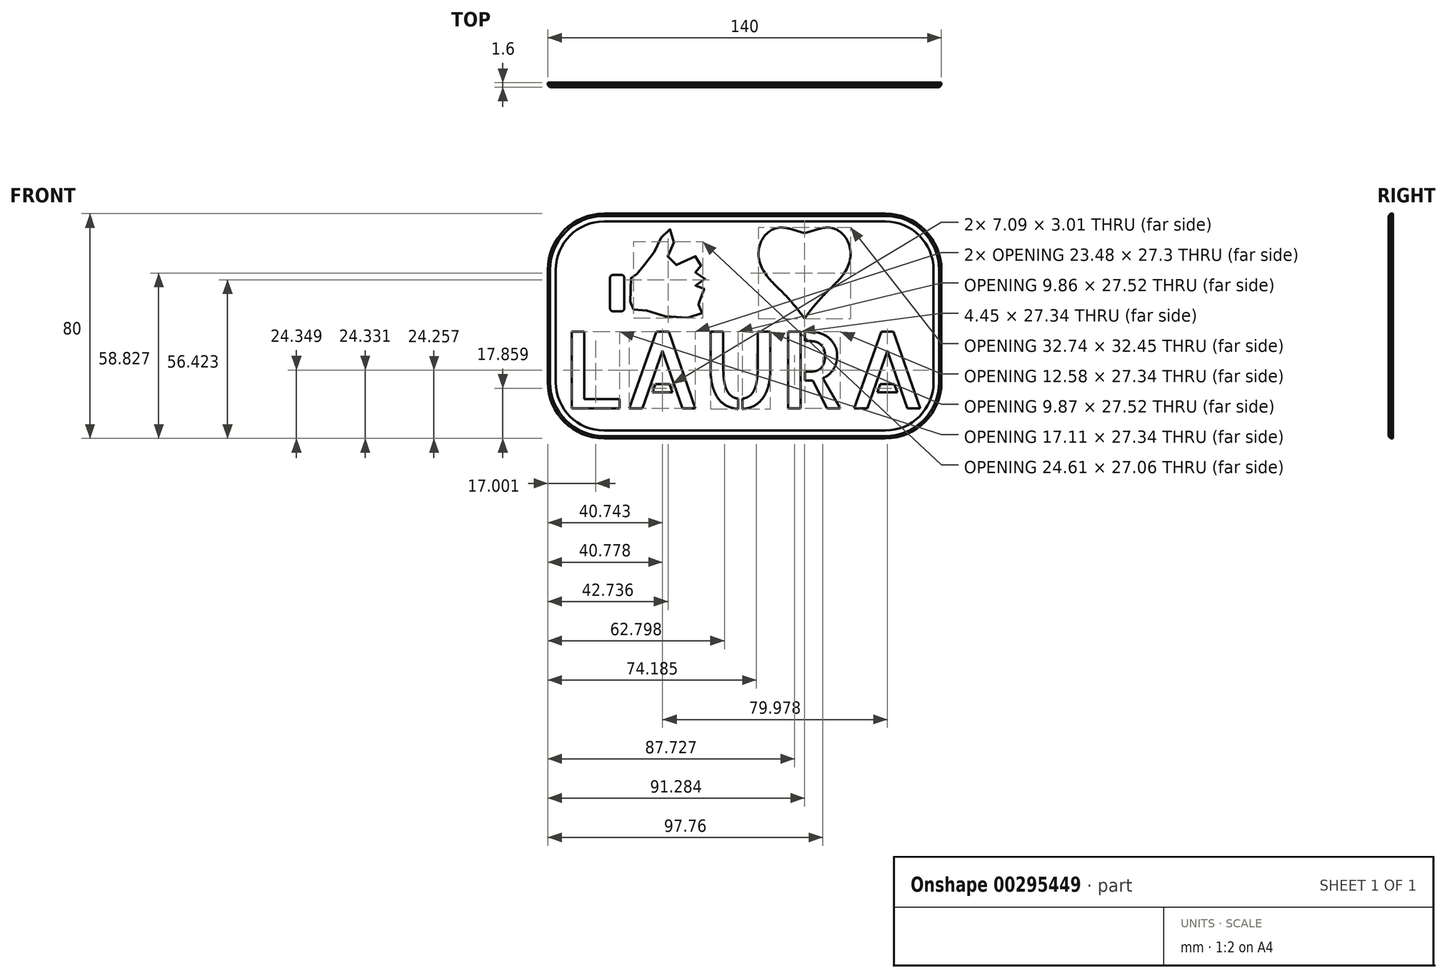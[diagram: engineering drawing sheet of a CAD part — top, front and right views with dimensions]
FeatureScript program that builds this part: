
annotation { "Feature Type Name" : "Feature", "Feature Type Description" : "" }
export const myFeature = defineFeature(function(context is Context, id is Id, definition is map)
    precondition{}
    {
        {
            var Q0;
            Q0=qCreatedBy(makeId("Front.planeOp"),FACE);
            var sketch = newSketch(context, id + "F0", { "sketchPlane" : qUnion([Q0])});
            skLineSegment(sketch, "E0.bottom", {"start": v(-70, 60) * mm, "end": v(70, 60) * mm});
            skLineSegment(sketch, "E0.top", {"start": v(-70, -20) * mm, "end": v(70, -20) * mm});
            skLineSegment(sketch, "E0.left", {"start": v(-70, 60) * mm, "end": v(-70, -20) * mm});
            skLineSegment(sketch, "E0.right", {"start": v(70, 60) * mm, "end": v(70, -20) * mm});
            skSolve(sketch);
        }
        {
            var Q0;
            Q0=qSketchRegion(id+"F0",true);
            extrude(context, id + "F1", {"entities" : qUnion([Q0]), "depth" : 1.6 * mm});
        }
        {
            var Q0;
            Q0=makeQuery(id+"F1.opExtrude","CAP_FACE",FACE,{"disambiguationData":[OSD([sQuery(id+"F0.wireOp",EDGE,"E0.bottom"),sQuery(id+"F0.wireOp",EDGE,"E0.top"),sQuery(id+"F0.wireOp",EDGE,"E0.left"),sQuery(id+"F0.wireOp",EDGE,"E0.right")])],"isStart":false});
            var sketch = newSketch(context, id + "F2", { "sketchPlane" : qUnion([Q0])});
            skText(sketch, "E1", { "text": "LAURA", "fontName": "AllertaStencil-Regular.ttf"});
            skText(sketch, "E2", { "text": "♥", "fontName": "NotoSansCJKjp-Regular.otf"});
            const initialGuessF2  = {"E1": [-0.065, -0.00932, 1, 0, 0.02735], "E2": [0.00184, 0.0241, 1, 0, 0.028]};
            skSetInitialGuess(sketch, initialGuessF2);
            skSolve(sketch);
        }
        {
            var Q0;
            Q0=qSketchRegion(id+"F2",true);
            extrude(context, id + "F3", {"entities" : qUnion([Q0]), "operationType" : NewBodyOperationType.REMOVE, "endBound" : BoundingType.THROUGH_ALL, "oppositeDirection" : true, "depth" : 25 * mm});
        }
        {
            var Q0;
            Q0=makeQuery(id+"F1.opExtrude","SWEPT_EDGE",EDGE,{"disambiguationData":[OSD([sQuery(id+"F0.wireOp",EDGE,"E0.top"),sQuery(id+"F0.wireOp",EDGE,"E0.right")])]});
            var Q1;
            Q1=makeQuery(id+"F1.opExtrude","SWEPT_EDGE",EDGE,{"disambiguationData":[OSD([sQuery(id+"F0.wireOp",EDGE,"E0.bottom"),sQuery(id+"F0.wireOp",EDGE,"E0.right")])]});
            var Q2;
            Q2=makeQuery(id+"F1.opExtrude","SWEPT_EDGE",EDGE,{"disambiguationData":[OSD([sQuery(id+"F0.wireOp",EDGE,"E0.top"),sQuery(id+"F0.wireOp",EDGE,"E0.left")])]});
            var Q3;
            Q3=makeQuery(id+"F1.opExtrude","SWEPT_EDGE",EDGE,{"disambiguationData":[OSD([sQuery(id+"F0.wireOp",EDGE,"E0.bottom"),sQuery(id+"F0.wireOp",EDGE,"E0.left")])]});
            fillet(context, id + "F4", {"entities" : qUnion([Q0, Q1, Q2, Q3]), "radius" : 20 * mm, "tangentPropagation" : true, "allowEdgeOverflow" : false});
        }
        {
            var Q0;
            Q0=makeQuery(id+"F1.opExtrude","CAP_EDGE",EDGE,{"disambiguationData":[OSD([sQuery(id+"F0.wireOp",EDGE,"E0.top")])],"isStart":false});
            chamfer(context, id + "F5", {"entities" : qUnion([Q0]), "width" : 0.8 * mm, "tangentPropagation" : true});
        }
        {
            var Q0;
            Q0=makeQuery(id+"F1.opExtrude","CAP_FACE",FACE,{"disambiguationData":[OSD([sQuery(id+"F0.wireOp",EDGE,"E0.bottom"),sQuery(id+"F0.wireOp",EDGE,"E0.top"),sQuery(id+"F0.wireOp",EDGE,"E0.left"),sQuery(id+"F0.wireOp",EDGE,"E0.right")])],"isStart":false});
            var sketch = newSketch(context, id + "F6", { "sketchPlane" : qUnion([Q0])});
            skLineSegment(sketch, "E3.0", {"start": v(-50, -17.2) * mm, "end": v(50, -17.2) * mm});
            skArc(sketch, "E3.1", {"start": v(-67.2, 0) * mm, "mid": v(-62.16, -12.16) * mm, "end": v(-50, -17.2) * mm});
            skArc(sketch, "E3.2", {"start": v(50, -17.2) * mm, "mid": v(62.16, -12.16) * mm, "end": v(67.2, 0) * mm});
            skLineSegment(sketch, "E3.3", {"start": v(-67.2, 40) * mm, "end": v(-67.2, 0) * mm});
            skLineSegment(sketch, "E3.4", {"start": v(67.2, 0) * mm, "end": v(67.2, 40) * mm});
            skArc(sketch, "E3.5", {"start": v(67.2, 40) * mm, "mid": v(62.16, 52.16) * mm, "end": v(50, 57.2) * mm});
            skLineSegment(sketch, "E3.6", {"start": v(50, 57.2) * mm, "end": v(-50, 57.2) * mm});
            skArc(sketch, "E3.7", {"start": v(-50, 57.2) * mm, "mid": v(-62.16, 52.16) * mm, "end": v(-67.2, 40) * mm});
            skSolve(sketch);
        }
        {
            var Q0;
            Q0=qSketchRegion(id+"F6",true);
            extrude(context, id + "F7", {"entities" : qUnion([Q0]), "operationType" : NewBodyOperationType.REMOVE, "oppositeDirection" : true, "depth" : 0.4 * mm});
        }
        {
            var Q0;
            Q0=makeQuery(id+"F7.boolean.opBoolean","COPY",FACE,{"derivedFrom":makeQuery(id+"F7.opExtrude","CAP_FACE",FACE,{"disambiguationData":[OSD([sQuery(id+"F6.wireOp",EDGE,"E3.0"),sQuery(id+"F6.wireOp",EDGE,"E3.1"),sQuery(id+"F6.wireOp",EDGE,"E3.2"),sQuery(id+"F6.wireOp",EDGE,"E3.3"),sQuery(id+"F6.wireOp",EDGE,"E3.4"),sQuery(id+"F6.wireOp",EDGE,"E3.5"),sQuery(id+"F6.wireOp",EDGE,"E3.6"),sQuery(id+"F6.wireOp",EDGE,"E3.7")])],"isStart":false})});
            var sketch = newSketch(context, id + "F8", { "sketchPlane" : qUnion([Q0])});
            skLineSegment(sketch, "E4", {"start": v(26.91, 54.7) * mm, "end": v(21.28, 53.06) * mm});
            skLineSegment(sketch, "E5", {"start": v(21.28, 53.06) * mm, "end": v(15.64, 54.7) * mm});
            skLineSegment(sketch, "E6", {"start": v(15.64, 54.7) * mm, "end": v(15.22, 47.04) * mm});
            skLineSegment(sketch, "E7", {"start": v(15.22, 47.04) * mm, "end": v(26.88, 46.4) * mm});
            skLineSegment(sketch, "E8", {"start": v(26.88, 46.4) * mm, "end": v(26.91, 54.7) * mm});
            skSolve(sketch);
        }
        {
            var Q0;
            Q0=qSketchRegion(id+"F8",true);
            extrude(context, id + "F9", {"entities" : qUnion([Q0]), "operationType" : NewBodyOperationType.REMOVE, "oppositeDirection" : true, "depth" : 25 * mm});
        }
        {
            var Q0;
            Q0=makeQuery(id+"F7.boolean.opBoolean","COPY",FACE,{"derivedFrom":makeQuery(id+"F7.opExtrude","CAP_FACE",FACE,{"disambiguationData":[OSD([sQuery(id+"F6.wireOp",EDGE,"E3.0"),sQuery(id+"F6.wireOp",EDGE,"E3.1"),sQuery(id+"F6.wireOp",EDGE,"E3.2"),sQuery(id+"F6.wireOp",EDGE,"E3.3"),sQuery(id+"F6.wireOp",EDGE,"E3.4"),sQuery(id+"F6.wireOp",EDGE,"E3.5"),sQuery(id+"F6.wireOp",EDGE,"E3.6"),sQuery(id+"F6.wireOp",EDGE,"E3.7")])],"isStart":false})});
            var sketch = newSketch(context, id + "F10", { "sketchPlane" : qUnion([Q0])});
            skFitSpline(sketch, "E9", {"points": [v(-39.57, 25.93) * mm, v(-40.32, 26.28) * mm, v(-40.6, 27.2) * mm, v(-40.34, 37.25) * mm, v(-40.19, 37.43) * mm, v(-39.33, 37.55) * mm, v(-37.33, 39.73) * mm, v(-35.58, 41.85) * mm, v(-32.38, 46.04) * mm, v(-30.1, 50.4) * mm, v(-27.74, 54.55) * mm, v(-24.91, 52.7) * mm, v(-26.13, 47.63) * mm, v(-27.4, 44) * mm, v(-24.51, 41.68) * mm, v(-16.78, 44.91) * mm, v(-15.22, 42.03) * mm, v(-17.82, 39.5) * mm, v(-17.82, 39.12) * mm, v(-14.65, 38.45) * mm, v(-14.82, 35.4) * mm, v(-17.49, 34.42) * mm, v(-17.49, 34.07) * mm, v(-14.53, 33.32) * mm, v(-14.59, 29.91) * mm, v(-17.58, 28.6) * mm, v(-17.53, 28.24) * mm, v(-14.53, 26.51) * mm, v(-15.34, 24.5) * mm, v(-19.6, 23) * mm, v(-30, 23.86) * mm, v(-36.28, 25.88) * mm, v(-39.57, 25.93) * mm]});
            skLineSegment(sketch, "E10.bottom", {"start": v(-43.8, 38.15) * mm, "end": v(-46.9, 38.15) * mm});
            skLineSegment(sketch, "E10.top", {"start": v(-43.8, 25.28) * mm, "end": v(-46.9, 25.28) * mm});
            skLineSegment(sketch, "E10.left", {"start": v(-42.8, 37.15) * mm, "end": v(-42.8, 26.28) * mm});
            skLineSegment(sketch, "E10.right", {"start": v(-47.9, 37.15) * mm, "end": v(-47.9, 26.28) * mm});
            skPoint(sketch, "E11.visualSharp", {"position": v(-42.8, 38.15) * mm});
            skArc(sketch, "E11.filletArc", {"start": v(-42.8, 37.15) * mm, "mid": v(-43.1, 37.86) * mm, "end": v(-43.8, 38.15) * mm});
            skPoint(sketch, "E12.visualSharp", {"position": v(-47.9, 38.15) * mm});
            skArc(sketch, "E12.filletArc", {"start": v(-46.9, 38.15) * mm, "mid": v(-47.6, 37.86) * mm, "end": v(-47.9, 37.15) * mm});
            skPoint(sketch, "E13.visualSharp", {"position": v(-47.9, 25.28) * mm});
            skArc(sketch, "E13.filletArc", {"start": v(-47.9, 26.28) * mm, "mid": v(-47.6, 25.57) * mm, "end": v(-46.9, 25.28) * mm});
            skPoint(sketch, "E14.visualSharp", {"position": v(-42.8, 25.28) * mm});
            skArc(sketch, "E14.filletArc", {"start": v(-43.8, 25.28) * mm, "mid": v(-43.1, 25.57) * mm, "end": v(-42.8, 26.28) * mm});
            skSolve(sketch);
        }
        {
            var Q0;
            Q0=qSketchRegion(id+"F10",true);
            extrude(context, id + "F11", {"entities" : qUnion([Q0]), "operationType" : NewBodyOperationType.REMOVE, "endBound" : BoundingType.THROUGH_ALL, "oppositeDirection" : true, "depth" : 25 * mm});
        }
    });
